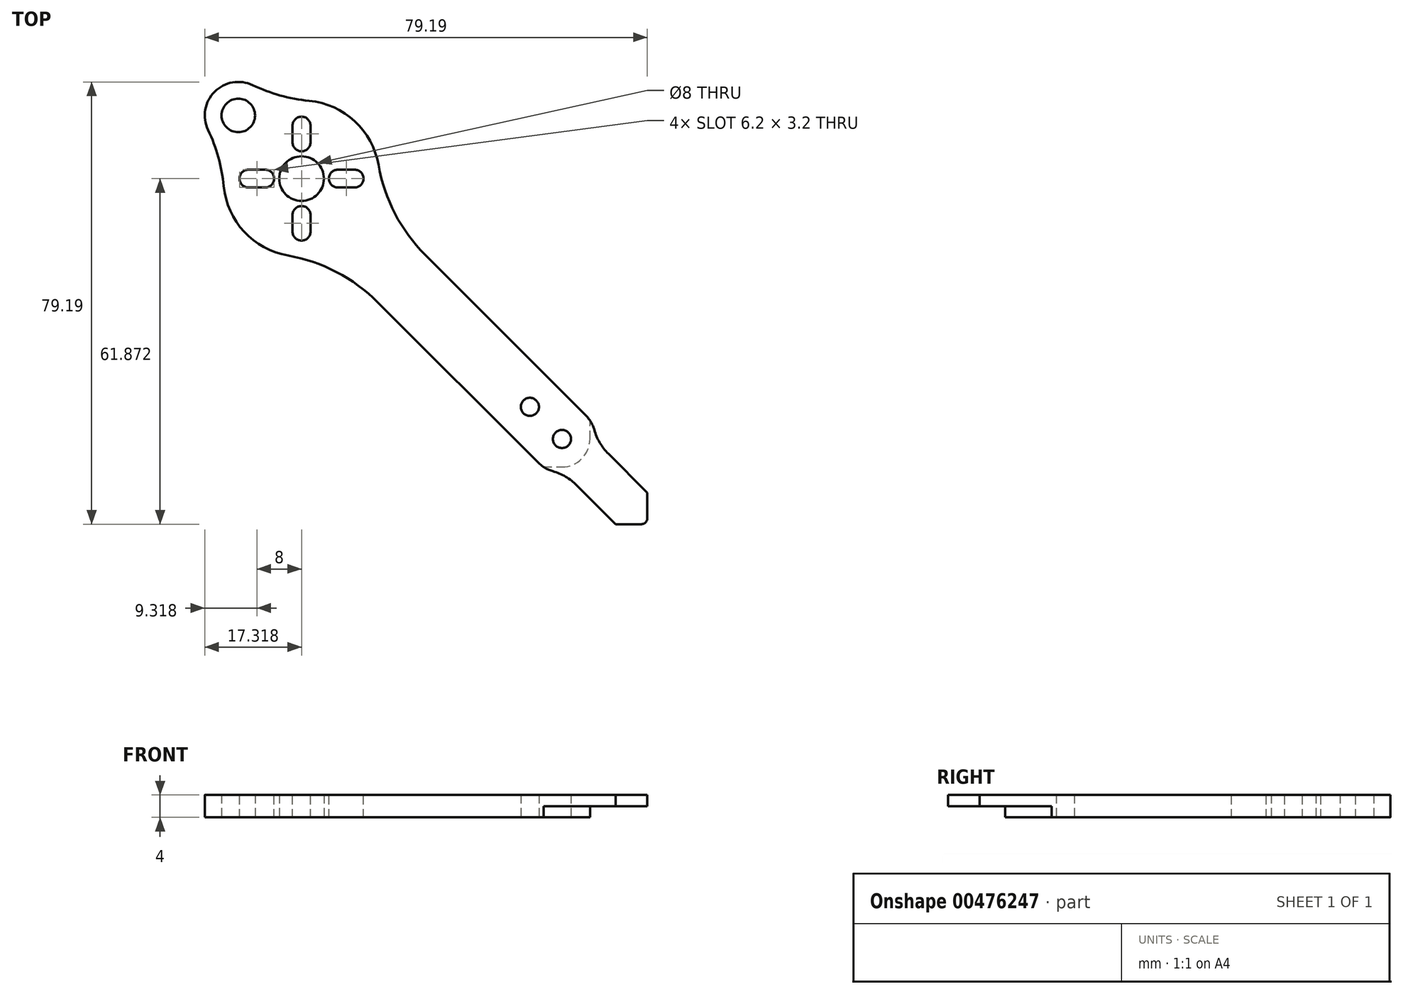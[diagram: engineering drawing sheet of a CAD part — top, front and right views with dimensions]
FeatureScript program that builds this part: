
annotation { "Feature Type Name" : "Feature", "Feature Type Description" : "" }
export const myFeature = defineFeature(function(context is Context, id is Id, definition is map)
    precondition{}
    {
        {
            var Q0;
            Q0=qCreatedBy(makeId("Top.planeOp"),FACE);
            var sketch = newSketch(context, id + "F0", { "sketchPlane" : qUnion([Q0])});
            skCircle(sketch, "E0", {"center": v(-15.25, 15.25) * mm, "radius": 1.63 * mm});
            skCircle(sketch, "E1", {"center": v(-21, 21) * mm, "radius": 1.63 * mm});
            skLineSegment(sketch, "E2", {"start": v(0, 0) * mm, "end": v(-61.87, 61.87) * mm, "construction": true});
            skLineSegment(sketch, "E3", {"start": v(-11, 19.5) * mm, "end": v(-39.74, 48.23) * mm});
            skLineSegment(sketch, "E4", {"start": v(-5.66, 0) * mm, "end": v(0, 0) * mm});
            skLineSegment(sketch, "E5", {"start": v(0, 0) * mm, "end": v(0, 5.66) * mm});
            skArc(sketch, "E6", {"start": v(-75.8, 60.54) * mm, "mid": v(-72.15, 52.36) * mm, "end": v(-64.28, 48.08) * mm});
            skArc(sketch, "E7", {"start": v(-70.6, 78.6) * mm, "mid": v(-77.43, 77.43) * mm, "end": v(-78.6, 70.6) * mm});
            skCircle(sketch, "E8", {"center": v(-73.19, 73.19) * mm, "radius": 3 * mm});
            skLineSegment(sketch, "E9", {"start": v(-61.87, 61.87) * mm, "end": v(-73.19, 73.19) * mm, "construction": true});
            skPoint(sketch, "E10.visualSharp", {"position": v(-67.39, 74.74) * mm});
            skArc(sketch, "E10.filletArc", {"start": v(-70.6, 78.6) * mm, "mid": v(-65.69, 76.76) * mm, "end": v(-60.54, 75.8) * mm});
            skPoint(sketch, "E11.visualSharp", {"position": v(-74.74, 67.39) * mm});
            skArc(sketch, "E11.filletArc", {"start": v(-75.8, 60.54) * mm, "mid": v(-76.76, 65.69) * mm, "end": v(-78.6, 70.6) * mm});
            skArc(sketch, "E12.trimOffspring", {"start": v(-48.08, 64.28) * mm, "mid": v(-52.36, 72.15) * mm, "end": v(-60.54, 75.8) * mm});
            skPoint(sketch, "E13.visualSharp", {"position": v(-48.68, 57.17) * mm});
            skArc(sketch, "E13.filletArc", {"start": v(-48.08, 64.28) * mm, "mid": v(-45.15, 55.6) * mm, "end": v(-39.74, 48.23) * mm});
            skArc(sketch, "E14.filletArc", {"start": v(-48.23, 39.74) * mm, "mid": v(-55.6, 45.15) * mm, "end": v(-64.28, 48.08) * mm});
            skCircle(sketch, "E15", {"center": v(-61.87, 61.87) * mm, "radius": 4 * mm});
            skLineSegment(sketch, "E16.trimOffspring", {"start": v(-19.5, 11) * mm, "end": v(-48.23, 39.74) * mm});
            skArc(sketch, "E17.trimOffspring", {"start": v(-19.5, 11) * mm, "mid": v(-18.3, 10.08) * mm, "end": v(-16.9, 9.48) * mm});
            skLineSegment(sketch, "E18", {"start": v(-5.66, 0) * mm, "end": v(-12.6, 6.94) * mm});
            skLineSegment(sketch, "E19", {"start": v(-6.94, 12.6) * mm, "end": v(0, 5.66) * mm});
            skArc(sketch, "E20.trimOffspring", {"start": v(-9.48, 16.9) * mm, "mid": v(-10.08, 18.3) * mm, "end": v(-11, 19.5) * mm});
            skPoint(sketch, "E21.orphan", {"position": v(0, 8.49) * mm});
            skPoint(sketch, "E22.visualSharp", {"position": v(-14.92, 9.26) * mm});
            skArc(sketch, "E22.filletArc", {"start": v(-12.6, 6.94) * mm, "mid": v(-14.6, 8.49) * mm, "end": v(-16.9, 9.48) * mm});
            skPoint(sketch, "E23.visualSharp", {"position": v(-9.26, 14.92) * mm});
            skArc(sketch, "E23.filletArc", {"start": v(-9.48, 16.9) * mm, "mid": v(-8.49, 14.6) * mm, "end": v(-6.94, 12.6) * mm});
            skCircle(sketch, "E24", {"center": v(61.87, 61.87) * mm, "radius": 51.75 * mm, "construction": true});
            skLineSegment(sketch, "E25", {"start": v(0, 0) * mm, "end": v(61.87, 61.87) * mm, "construction": true});
            skCircle(sketch, "E26.MirrorC", {"center": v(-61.87, 61.87) * mm, "radius": 51.75 * mm, "construction": true});
            skSolve(sketch);
        }
        {
            var Q0;
            Q0=qSketchRegion(id+"F0",true);
            extrude(context, id + "F1", {"entities" : qUnion([Q0]), "depth" : 4 * mm});
        }
        {
            var Q0;
            Q0=makeQuery(id+"F1.opExtrude","CAP_FACE",FACE,{"disambiguationData":[OSD([sQuery(id+"F0.wireOp",EDGE,"ELmgnBSW-vcTX-69ba-dwwi-cACzyNvr3Jda"),sQuery(id+"F0.wireOp",EDGE,"E0"),sQuery(id+"F0.wireOp",EDGE,"E1"),sQuery(id+"F0.wireOp",EDGE,"wzC1F6xg-fGIV-3KpO-c9gR-K1YJSPa7NM8s"),sQuery(id+"F0.wireOp",EDGE,"E3"),sQuery(id+"F0.wireOp",EDGE,"FoUFOdND-4TSw-zWgQ-ILiy-lV2VMV41Ndkk"),sQuery(id+"F0.wireOp",EDGE,"gZyNtGtT-cGv0-NfnX-XPpx-gTdD2O9JXBFj"),sQuery(id+"F0.wireOp",EDGE,"AxQfXuDg-QIAQ-o6Jz-UGCb-lciMLiFu8Ysp"),sQuery(id+"F0.wireOp",EDGE,"495c5933-9560-4cef-81c8-4e8a0d039e08.trimOffspring"),sQuery(id+"F0.wireOp",EDGE,"E4"),sQuery(id+"F0.wireOp",EDGE,"E5"),sQuery(id+"F0.wireOp",EDGE,"ef546a75-4e02-40f2-ac6e-af8522daafdd.filletArc"),sQuery(id+"F0.wireOp",EDGE,"2512e942-d075-422c-a12b-7db6a64d2190.filletArc"),sQuery(id+"F0.wireOp",EDGE,"E6"),sQuery(id+"F0.wireOp",EDGE,"E7"),sQuery(id+"F0.wireOp",EDGE,"E8"),sQuery(id+"F0.wireOp",EDGE,"E10.filletArc"),sQuery(id+"F0.wireOp",EDGE,"E11.filletArc"),sQuery(id+"F0.wireOp",EDGE,"E12.trimOffspring"),sQuery(id+"F0.wireOp",EDGE,"E13.filletArc"),sQuery(id+"F0.wireOp",EDGE,"E14.filletArc"),sQuery(id+"F0.wireOp",EDGE,"E15")])],"isStart":false});
            var sketch = newSketch(context, id + "F2", { "sketchPlane" : qUnion([Q0])});
            skLineSegment(sketch, "E27", {"start": v(-61.87, 61.87) * mm, "end": v(-55.37, 61.87) * mm, "construction": true});
            skLineSegment(sketch, "E28", {"start": v(-61.87, 61.87) * mm, "end": v(0, 0) * mm, "construction": true});
            skLineSegment(sketch, "E29", {"start": v(-55.37, 61.87) * mm, "end": v(-52.37, 61.87) * mm, "construction": true});
            skArc(sketch, "E30.0.startCap", {"start": v(-55.37, 60.27) * mm, "mid": v(-56.97, 61.87) * mm, "end": v(-55.37, 63.47) * mm});
            skArc(sketch, "E30.0.endCap", {"start": v(-52.37, 63.47) * mm, "mid": v(-50.77, 61.87) * mm, "end": v(-52.37, 60.27) * mm});
            skLineSegment(sketch, "E30.0.left", {"start": v(-55.37, 63.47) * mm, "end": v(-52.37, 63.47) * mm});
            skLineSegment(sketch, "E30.0.right", {"start": v(-55.37, 60.27) * mm, "end": v(-52.37, 60.27) * mm});
            skLineSegment(sketch, "E31.1.0", {"start": v(-63.47, 68.37) * mm, "end": v(-63.47, 71.37) * mm});
            skArc(sketch, "E31.1.1", {"start": v(-60.27, 68.37) * mm, "mid": v(-61.87, 66.77) * mm, "end": v(-63.47, 68.37) * mm});
            skLineSegment(sketch, "E31.1.2", {"start": v(-60.27, 68.37) * mm, "end": v(-60.27, 71.37) * mm});
            skArc(sketch, "E31.1.3", {"start": v(-63.47, 71.37) * mm, "mid": v(-61.87, 72.97) * mm, "end": v(-60.27, 71.37) * mm});
            skLineSegment(sketch, "E31.2.0", {"start": v(-68.37, 60.27) * mm, "end": v(-71.37, 60.27) * mm});
            skArc(sketch, "E31.2.1", {"start": v(-68.37, 63.47) * mm, "mid": v(-66.77, 61.87) * mm, "end": v(-68.37, 60.27) * mm});
            skLineSegment(sketch, "E31.2.2", {"start": v(-68.37, 63.47) * mm, "end": v(-71.37, 63.47) * mm});
            skArc(sketch, "E31.2.3", {"start": v(-71.37, 60.27) * mm, "mid": v(-72.97, 61.87) * mm, "end": v(-71.37, 63.47) * mm});
            skLineSegment(sketch, "E31.3.0", {"start": v(-60.27, 55.37) * mm, "end": v(-60.27, 52.37) * mm});
            skArc(sketch, "E31.3.1", {"start": v(-63.47, 55.37) * mm, "mid": v(-61.87, 56.97) * mm, "end": v(-60.27, 55.37) * mm});
            skLineSegment(sketch, "E31.3.2", {"start": v(-63.47, 55.37) * mm, "end": v(-63.47, 52.37) * mm});
            skArc(sketch, "E31.3.3", {"start": v(-60.27, 52.37) * mm, "mid": v(-61.87, 50.77) * mm, "end": v(-63.47, 52.37) * mm});
            skPoint(sketch, "E31.center", {"position": v(-61.87, 61.87) * mm});
            skSolve(sketch);
        }
        {
            var Q0;
            Q0=qSketchRegion(id+"F2",true);
            extrude(context, id + "F3", {"entities" : qUnion([Q0]), "operationType" : NewBodyOperationType.REMOVE, "oppositeDirection" : true, "depth" : 25 * mm});
        }
        {
            var Q0;
            Q0=makeQuery(id+"F1.opExtrude","CAP_FACE",FACE,{"disambiguationData":[OSD([sQuery(id+"F0.wireOp",EDGE,"E0"),sQuery(id+"F0.wireOp",EDGE,"E1"),sQuery(id+"F0.wireOp",EDGE,"E3"),sQuery(id+"F0.wireOp",EDGE,"E4"),sQuery(id+"F0.wireOp",EDGE,"E5"),sQuery(id+"F0.wireOp",EDGE,"E6"),sQuery(id+"F0.wireOp",EDGE,"E7"),sQuery(id+"F0.wireOp",EDGE,"E8"),sQuery(id+"F0.wireOp",EDGE,"E10.filletArc"),sQuery(id+"F0.wireOp",EDGE,"E11.filletArc"),sQuery(id+"F0.wireOp",EDGE,"E12.trimOffspring"),sQuery(id+"F0.wireOp",EDGE,"E13.filletArc"),sQuery(id+"F0.wireOp",EDGE,"E14.filletArc"),sQuery(id+"F0.wireOp",EDGE,"E15"),sQuery(id+"F0.wireOp",EDGE,"E16.trimOffspring"),sQuery(id+"F0.wireOp",EDGE,"E17.trimOffspring"),sQuery(id+"F0.wireOp",EDGE,"E18"),sQuery(id+"F0.wireOp",EDGE,"E19"),sQuery(id+"F0.wireOp",EDGE,"E20.trimOffspring"),sQuery(id+"F0.wireOp",EDGE,"E22.filletArc"),sQuery(id+"F0.wireOp",EDGE,"E23.filletArc")])],"isStart":true});
            var sketch = newSketch(context, id + "F4", { "sketchPlane" : qUnion([Q0])});
            skLineSegment(sketch, "E32", {"start": v(-20, 0) * mm, "end": v(-20, -10.25) * mm});
            skLineSegment(sketch, "E33", {"start": v(-20, -10.25) * mm, "end": v(-15.25, -10.25) * mm});
            skLineSegment(sketch, "E34", {"start": v(0, -20) * mm, "end": v(0, 0) * mm});
            skLineSegment(sketch, "E35", {"start": v(-20, 0) * mm, "end": v(0, 0) * mm});
            skLineSegment(sketch, "E36", {"start": v(-10.25, -15.25) * mm, "end": v(-10.25, -20) * mm});
            skLineSegment(sketch, "E37", {"start": v(-10.25, -20) * mm, "end": v(0, -20) * mm});
            skPoint(sketch, "E38.visualSharp", {"position": v(-10.25, -10.25) * mm});
            skArc(sketch, "E38.filletArc", {"start": v(-10.25, -15.25) * mm, "mid": v(-11.71, -11.71) * mm, "end": v(-15.25, -10.25) * mm});
            skSolve(sketch);
        }
        {
            var Q0;
            Q0=qSketchRegion(id+"F4",true);
            extrude(context, id + "F5", {"entities" : qUnion([Q0]), "operationType" : NewBodyOperationType.REMOVE, "oppositeDirection" : true, "depth" : 2 * mm, "offsetDistance" : 25 * mm});
        }
        {
            var Q0;
            Q0=makeQuery(id+"F1.opExtrude","SWEPT_EDGE",EDGE,{"disambiguationData":[OSD([sQuery(id+"F0.wireOp",EDGE,"E4"),sQuery(id+"F0.wireOp",EDGE,"E5")])]});
            fillet(context, id + "F6", {"entities" : qUnion([Q0]), "radius" : 1 * mm, "tangentPropagation" : true, "allowEdgeOverflow" : false});
        }
    });
